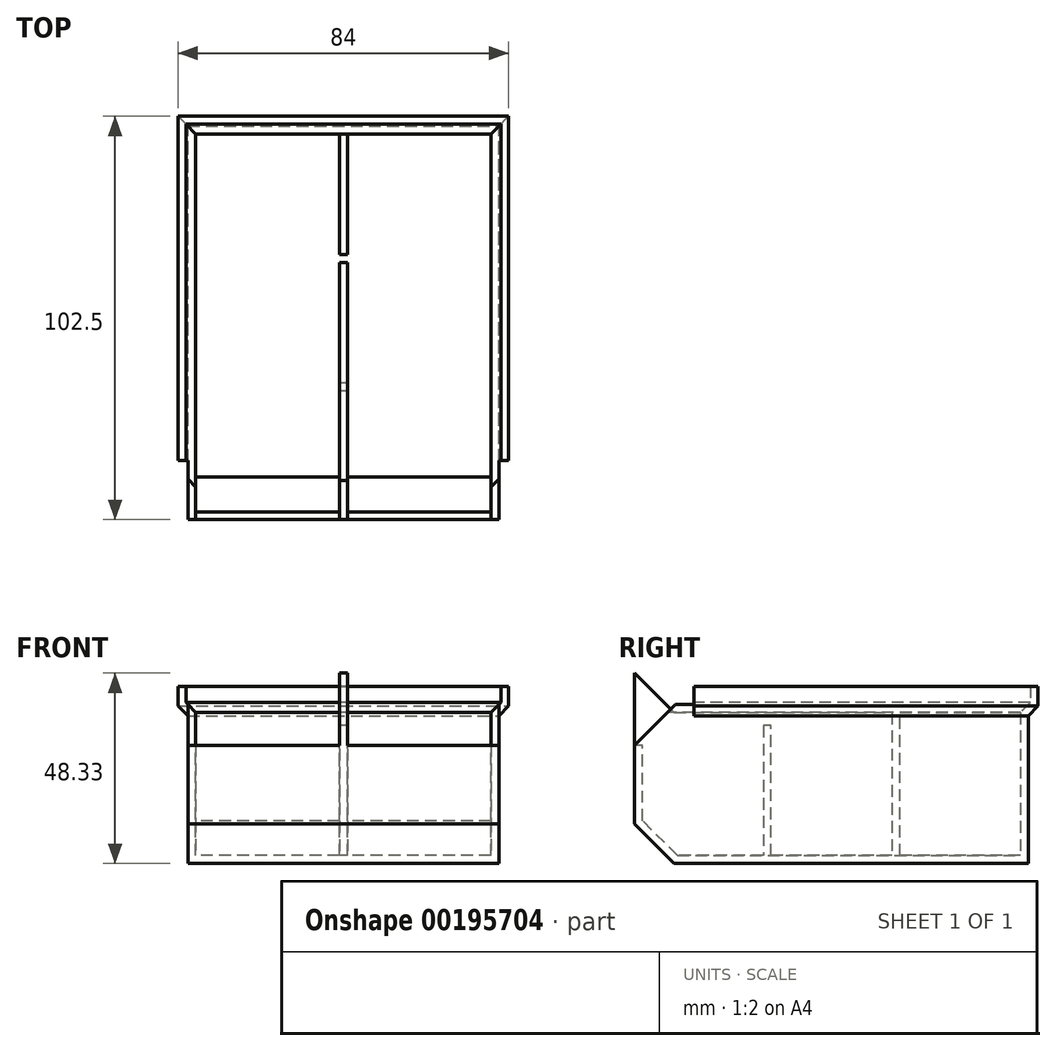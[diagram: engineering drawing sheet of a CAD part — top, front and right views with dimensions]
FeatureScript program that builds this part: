
annotation { "Feature Type Name" : "Feature", "Feature Type Description" : "" }
export const myFeature = defineFeature(function(context is Context, id is Id, definition is map)
    precondition{}
    {
        {
            var Q0;
            Q0=qCreatedBy(makeId("Right.planeOp"),FACE);
            var sketch = newSketch(context, id + "F0", { "sketchPlane" : qUnion([Q0])});
            skLineSegment(sketch, "E0.bottom", {"start": v(0, 0) * mm, "end": v(100, 0) * mm});
            skLineSegment(sketch, "E0.top", {"start": v(0, 45) * mm, "end": v(100, 45) * mm});
            skLineSegment(sketch, "E0.left", {"start": v(0, 0) * mm, "end": v(0, 45) * mm});
            skLineSegment(sketch, "E0.right", {"start": v(100, 0) * mm, "end": v(100, 45) * mm});
            skLineSegment(sketch, "E1", {"start": v(0, 10) * mm, "end": v(10, 0) * mm});
            skLineSegment(sketch, "E2", {"start": v(15, 45) * mm, "end": v(0, 30) * mm});
            skLineSegment(sketch, "E3", {"start": v(100, 45) * mm, "end": v(102.5, 45) * mm});
            skLineSegment(sketch, "E4", {"start": v(102.5, 45) * mm, "end": v(102.5, 40) * mm});
            skLineSegment(sketch, "E5", {"start": v(102.5, 40) * mm, "end": v(100, 37.5) * mm});
            skSolve(sketch);
        }
        {
            var Q0;
            {var subQ4=sQuery(id+"F0.wireOp",EDGE,"E1");Q0=makeQuery(id+"F0.imprint","IMPRINT",FACE,{"disambiguationData":[TD([[makeQuery(id+"F0.imprint","IMPRINT",EDGE,{"derivedFrom":subQ4}),1.0]])]});}
            var Q1;
            {var subQ0=sQuery(id+"F0.wireOp",EDGE,"E3");Q1=makeQuery(id+"F0.imprint","IMPRINT",FACE,{"disambiguationData":[TD([[makeQuery(id+"F0.imprint","IMPRINT",EDGE,{"derivedFrom":subQ0}),-1.0]])]});}
            extrude(context, id + "F1", {"entities" : qUnion([Q0, Q1]), "oppositeDirection" : true, "depth" : 2 * mm});
        }
        {
            var Q0;
            Q0=makeQuery(id+"F1.opExtrude","CAP_FACE",FACE,{"disambiguationData":[OSD([sQuery(id+"F0.wireOp",EDGE,"E0.bottom"),sQuery(id+"F0.wireOp",EDGE,"E0.top"),sQuery(id+"F0.wireOp",EDGE,"E0.left"),sQuery(id+"F0.wireOp",EDGE,"E0.right"),sQuery(id+"F0.wireOp",EDGE,"E1"),sQuery(id+"F0.wireOp",EDGE,"E2"),sQuery(id+"F0.wireOp",EDGE,"E3"),sQuery(id+"F0.wireOp",EDGE,"E4"),sQuery(id+"F0.wireOp",EDGE,"E5")])],"isStart":true});
            var sketch = newSketch(context, id + "F2", { "sketchPlane" : qUnion([Q0])});
            skLineSegment(sketch, "E6", {"start": v(0, 30) * mm, "end": v(2, 30) * mm});
            skLineSegment(sketch, "E7", {"start": v(2, 30) * mm, "end": v(2, 10.83) * mm});
            skLineSegment(sketch, "E8", {"start": v(2, 10.83) * mm, "end": v(10.83, 2) * mm});
            skLineSegment(sketch, "E9", {"start": v(10.83, 2) * mm, "end": v(98, 2) * mm});
            skLineSegment(sketch, "E10", {"start": v(98, 2) * mm, "end": v(98, 38.33) * mm});
            skLineSegment(sketch, "E11", {"start": v(98, 38.33) * mm, "end": v(100.5, 40.83) * mm});
            skPoint(sketch, "E12.0", {"position": v(0, 20) * mm});
            skLineSegment(sketch, "E13.0", {"start": v(0, 10) * mm, "end": v(0, 30) * mm});
            skLineSegment(sketch, "E14.0", {"start": v(0, 10) * mm, "end": v(10, 0) * mm});
            skLineSegment(sketch, "E15.0", {"start": v(10, 0) * mm, "end": v(100, 0) * mm});
            skLineSegment(sketch, "E16.0", {"start": v(100, 0) * mm, "end": v(100, 37.5) * mm});
            skPoint(sketch, "E17.0", {"position": v(101.25, 38.75) * mm});
            skPoint(sketch, "E18.0", {"position": v(102.5, 42.5) * mm});
            skLineSegment(sketch, "E19.0", {"start": v(102.5, 45) * mm, "end": v(102.5, 40) * mm});
            skLineSegment(sketch, "E20.0", {"start": v(102.5, 40) * mm, "end": v(100, 37.5) * mm});
            skLineSegment(sketch, "E21.0", {"start": v(15, 45) * mm, "end": v(102.5, 45) * mm});
            skLineSegment(sketch, "E22", {"start": v(100.5, 40.83) * mm, "end": v(100.5, 45) * mm});
            skLineSegment(sketch, "E23.bottom", {"start": v(32.67, 2) * mm, "end": v(34.67, 2) * mm});
            skLineSegment(sketch, "E23.top", {"start": v(32.67, 35) * mm, "end": v(34.67, 35) * mm});
            skLineSegment(sketch, "E23.left", {"start": v(32.67, 2) * mm, "end": v(32.67, 35) * mm});
            skLineSegment(sketch, "E23.right", {"start": v(34.67, 2) * mm, "end": v(34.67, 35) * mm});
            skLineSegment(sketch, "E24.bottom", {"start": v(65.33, 2) * mm, "end": v(67.33, 2) * mm});
            skLineSegment(sketch, "E24.top", {"start": v(65.33, 40) * mm, "end": v(67.33, 40) * mm});
            skLineSegment(sketch, "E24.left", {"start": v(65.33, 2) * mm, "end": v(65.33, 40) * mm});
            skLineSegment(sketch, "E24.right", {"start": v(67.33, 2) * mm, "end": v(67.33, 40) * mm});
            skSolve(sketch);
        }
        {
            var Q0;
            Q0=makeQuery(id+"F2.imprint","IMPRINT",FACE,{"disambiguationData":[TD([[makeQuery(id+"F2.imprint","IMPRINT",EDGE,{"derivedFrom":sQuery(id+"F2.wireOp",EDGE,"E6")}),-1.0]])]});
            var Q1;
            Q1=makeQuery(id+"F2.imprint","IMPRINT",FACE,{"disambiguationData":[TD([[makeQuery(id+"F2.imprint","IMPRINT",EDGE,{"derivedFrom":sQuery(id+"F2.wireOp",EDGE,"E23.bottom")}),1.0]])]});
            var Q2;
            Q2=makeQuery(id+"F2.imprint","IMPRINT",FACE,{"disambiguationData":[TD([[makeQuery(id+"F2.imprint","IMPRINT",EDGE,{"derivedFrom":sQuery(id+"F2.wireOp",EDGE,"E24.bottom")}),1.0]])]});
            extrude(context, id + "F3", {"entities" : qUnion([Q0, Q1, Q2]), "operationType" : NewBodyOperationType.ADD, "depth" : 75 * mm});
        }
        {
            var Q0;
            Q0=makeQuery(id+"F3.opExtrude","CAP_FACE",FACE,{"disambiguationData":[OSD([sQuery(id+"F2.wireOp",EDGE,"E6"),sQuery(id+"F2.wireOp",EDGE,"E7"),sQuery(id+"F2.wireOp",EDGE,"E8"),sQuery(id+"F2.wireOp",EDGE,"E9"),sQuery(id+"F2.wireOp",EDGE,"E10"),sQuery(id+"F2.wireOp",EDGE,"E11"),sQuery(id+"F2.wireOp",EDGE,"E13.0"),sQuery(id+"F2.wireOp",EDGE,"E14.0"),sQuery(id+"F2.wireOp",EDGE,"E15.0"),sQuery(id+"F2.wireOp",EDGE,"E16.0"),sQuery(id+"F2.wireOp",EDGE,"E19.0"),sQuery(id+"F2.wireOp",EDGE,"E20.0"),sQuery(id+"F2.wireOp",EDGE,"E21.0"),sQuery(id+"F2.wireOp",EDGE,"E22"),sQuery(id+"F2.wireOp",EDGE,"E23.top"),sQuery(id+"F2.wireOp",EDGE,"E23.left"),sQuery(id+"F2.wireOp",EDGE,"E23.right"),sQuery(id+"F2.wireOp",EDGE,"E24.top"),sQuery(id+"F2.wireOp",EDGE,"E24.left"),sQuery(id+"F2.wireOp",EDGE,"E24.right")])],"isStart":false});
            var sketch = newSketch(context, id + "F4", { "sketchPlane" : qUnion([Q0])});
            skLineSegment(sketch, "E25.0", {"start": v(15, 45) * mm, "end": v(0, 30) * mm});
            skLineSegment(sketch, "E26.0", {"start": v(15, 45) * mm, "end": v(100.5, 45) * mm});
            skLineSegment(sketch, "E27.0", {"start": v(100.5, 45) * mm, "end": v(102.5, 45) * mm});
            skLineSegment(sketch, "E28.0", {"start": v(102.5, 45) * mm, "end": v(102.5, 40) * mm});
            skLineSegment(sketch, "E29.0", {"start": v(102.5, 40) * mm, "end": v(100, 37.5) * mm});
            skLineSegment(sketch, "E30.0", {"start": v(100, 0) * mm, "end": v(100, 37.5) * mm});
            skLineSegment(sketch, "E31.0", {"start": v(10, 0) * mm, "end": v(100, 0) * mm});
            skLineSegment(sketch, "E32.0", {"start": v(0, 10) * mm, "end": v(10, 0) * mm});
            skLineSegment(sketch, "E33.0", {"start": v(0, 10) * mm, "end": v(0, 30) * mm});
            skSolve(sketch);
        }
        {
            var Q0;
            Q0 = qSketchRegion(id + "F4", true);
            extrude(context, id + "F5", {"entities" : qUnion([Q0]), "operationType" : NewBodyOperationType.ADD, "depth" : 2 * mm});
        }
        {
            var Q0;
            Q0=makeQuery(id+"F5.boolean.opBoolean","MERGE",FACE,{"derivedFrom":[makeQuery(id+"F3.boolean.opBoolean","MERGE",FACE,{"derivedFrom":[makeQuery(id+"F1.opExtrude","SWEPT_FACE",FACE,{"disambiguationData":[OSD([sQuery(id+"F0.wireOp",EDGE,"E0.top"),sQuery(id+"F0.wireOp",EDGE,"E3")])]}),makeQuery(id+"F3.opExtrude","SWEPT_FACE",FACE,{"disambiguationData":[OSD([sQuery(id+"F2.wireOp",EDGE,"E21.0")])]})]}),makeQuery(id+"F5.opExtrude","SWEPT_FACE",FACE,{"disambiguationData":[OSD([sQuery(id+"F4.wireOp",EDGE,"E26.0"),sQuery(id+"F4.wireOp",EDGE,"E27.0")])]})]});
            var sketch = newSketch(context, id + "F6", { "sketchPlane" : qUnion([Q0])});
            skLineSegment(sketch, "E34.bottom", {"start": v(-2, 102.5) * mm, "end": v(-4.5, 102.5) * mm});
            skLineSegment(sketch, "E34.top", {"start": v(-2, 15) * mm, "end": v(-4.5, 15) * mm});
            skLineSegment(sketch, "E34.left", {"start": v(-2, 102.5) * mm, "end": v(-2, 15) * mm});
            skLineSegment(sketch, "E34.right", {"start": v(-4.5, 102.5) * mm, "end": v(-4.5, 15) * mm});
            skLineSegment(sketch, "E35.bottom", {"start": v(77, 102.5) * mm, "end": v(79.5, 102.5) * mm});
            skLineSegment(sketch, "E35.top", {"start": v(77, 15) * mm, "end": v(79.5, 15) * mm});
            skLineSegment(sketch, "E35.left", {"start": v(77, 102.5) * mm, "end": v(77, 15) * mm});
            skLineSegment(sketch, "E35.right", {"start": v(79.5, 102.5) * mm, "end": v(79.5, 15) * mm});
            skSolve(sketch);
        }
        {
            var Q0;
            Q0 = qSketchRegion(id + "F6", true);
            extrude(context, id + "F7", {"entities" : qUnion([Q0]), "operationType" : NewBodyOperationType.ADD, "oppositeDirection" : true, "depth" : 7.5 * mm});
        }
        {
            var Q0;
            Q0=makeQuery(id+"F7.boolean.opBoolean","MERGE",FACE,{"derivedFrom":[makeQuery(id+"F5.boolean.opBoolean","MERGE",FACE,{"derivedFrom":[makeQuery(id+"F3.boolean.opBoolean","MERGE",FACE,{"derivedFrom":[makeQuery(id+"F1.opExtrude","SWEPT_FACE",FACE,{"disambiguationData":[OSD([sQuery(id+"F0.wireOp",EDGE,"E4")])]}),makeQuery(id+"F3.opExtrude","SWEPT_FACE",FACE,{"disambiguationData":[OSD([sQuery(id+"F2.wireOp",EDGE,"E19.0")])]})]}),makeQuery(id+"F5.opExtrude","SWEPT_FACE",FACE,{"disambiguationData":[OSD([sQuery(id+"F4.wireOp",EDGE,"E28.0")])]})]}),makeQuery(id+"F7.opExtrude","SWEPT_FACE",FACE,{"disambiguationData":[OSD([sQuery(id+"F6.wireOp",EDGE,"E34.bottom")])]}),makeQuery(id+"F7.opExtrude","SWEPT_FACE",FACE,{"disambiguationData":[OSD([sQuery(id+"F6.wireOp",EDGE,"E35.bottom")])]})]});
            var sketch = newSketch(context, id + "F8", { "sketchPlane" : qUnion([Q0])});
            skLineSegment(sketch, "E36", {"start": v(-77, 37.5) * mm, "end": v(-79.5, 40) * mm});
            skLineSegment(sketch, "E37", {"start": v(2, 37.5) * mm, "end": v(4.5, 40) * mm});
            skLineSegment(sketch, "E38.0", {"start": v(-79.5, 37.5) * mm, "end": v(-79.5, 45) * mm});
            skLineSegment(sketch, "E39.0", {"start": v(-77, 37.5) * mm, "end": v(-79.5, 37.5) * mm});
            skLineSegment(sketch, "E40.0", {"start": v(2, 37.5) * mm, "end": v(4.5, 37.5) * mm});
            skLineSegment(sketch, "E41.0", {"start": v(4.5, 37.5) * mm, "end": v(4.5, 45) * mm});
            skSolve(sketch);
        }
        {
            var Q0;
            {var subQ0=sQuery(id+"F8.wireOp",EDGE,"E36");Q0=makeQuery(id+"F8.imprint","IMPRINT",FACE,{"disambiguationData":[TD([[makeQuery(id+"F8.imprint","IMPRINT",EDGE,{"derivedFrom":subQ0}),1.0]])]});}
            var Q1;
            {var subQ0=sQuery(id+"F8.wireOp",EDGE,"E37");Q1=makeQuery(id+"F8.imprint","IMPRINT",FACE,{"disambiguationData":[TD([[makeQuery(id+"F8.imprint","IMPRINT",EDGE,{"derivedFrom":subQ0}),-1.0]])]});}
            extrude(context, id + "F9", {"entities" : qUnion([Q0, Q1]), "operationType" : NewBodyOperationType.REMOVE, "endBound" : BoundingType.THROUGH_ALL, "oppositeDirection" : true, "depth" : 25 * mm});
        }
        {
            var Q0;
            Q0=makeQuery(id+"F7.opExtrude","SWEPT_FACE",FACE,{"disambiguationData":[OSD([sQuery(id+"F6.wireOp",EDGE,"E35.right")])]});
            var sketch = newSketch(context, id + "F10", { "sketchPlane" : qUnion([Q0])});
            skLineSegment(sketch, "E42.0", {"start": v(100, 0) * mm, "end": v(100, 37.5) * mm});
            skLineSegment(sketch, "E43.0", {"start": v(15, 37.5) * mm, "end": v(100, 37.5) * mm});
            skLineSegment(sketch, "E44.0", {"start": v(102.5, 37.5) * mm, "end": v(102.5, 40) * mm});
            skLineSegment(sketch, "E45.0", {"start": v(100, 37.5) * mm, "end": v(102.5, 37.5) * mm});
            skLineSegment(sketch, "E46", {"start": v(102.5, 40) * mm, "end": v(100, 37.5) * mm});
            skSolve(sketch);
        }
        {
            var Q0;
            Q0=makeQuery(id+"F10.imprint","IMPRINT",FACE,{"disambiguationData":[TD([[makeQuery(id+"F10.imprint","IMPRINT",EDGE,{"derivedFrom":sQuery(id+"F10.wireOp",EDGE,"E44.0")}),1.0]])]});
            extrude(context, id + "F11", {"entities" : qUnion([Q0]), "operationType" : NewBodyOperationType.REMOVE, "endBound" : BoundingType.THROUGH_ALL, "oppositeDirection" : true, "depth" : 25 * mm});
        }
        {
            var Q0;
            Q0=makeQuery(id+"F5.boolean.opBoolean","MERGE",FACE,{"derivedFrom":[makeQuery(id+"F3.boolean.opBoolean","MERGE",FACE,{"derivedFrom":[makeQuery(id+"F1.opExtrude","SWEPT_FACE",FACE,{"disambiguationData":[OSD([sQuery(id+"F0.wireOp",EDGE,"E0.left")])]}),makeQuery(id+"F3.opExtrude","SWEPT_FACE",FACE,{"disambiguationData":[OSD([sQuery(id+"F2.wireOp",EDGE,"E13.0")])]})]}),makeQuery(id+"F5.opExtrude","SWEPT_FACE",FACE,{"disambiguationData":[OSD([sQuery(id+"F4.wireOp",EDGE,"E33.0")])]})]});
            var sketch = newSketch(context, id + "F12", { "sketchPlane" : qUnion([Q0])});
            skLineSegment(sketch, "E47.0", {"start": v(-4.5, 40) * mm, "end": v(-4.5, 45) * mm});
            skLineSegment(sketch, "E48.0", {"start": v(-2, 37.5) * mm, "end": v(-4.5, 40) * mm});
            skLineSegment(sketch, "E49.0", {"start": v(75, 45) * mm, "end": v(0, 45) * mm});
            skLineSegment(sketch, "E50.0", {"start": v(-2, 45) * mm, "end": v(0, 45) * mm});
            skLineSegment(sketch, "E51.0", {"start": v(-2, 45) * mm, "end": v(-4.5, 45) * mm});
            skLineSegment(sketch, "E52.0", {"start": v(79.5, 40) * mm, "end": v(77, 37.5) * mm});
            skLineSegment(sketch, "E53.0", {"start": v(79.5, 40) * mm, "end": v(79.5, 45) * mm});
            skLineSegment(sketch, "E54.0", {"start": v(77, 45) * mm, "end": v(79.5, 45) * mm});
            skLineSegment(sketch, "E55.0", {"start": v(77, 45) * mm, "end": v(75, 45) * mm});
            skLineSegment(sketch, "E56", {"start": v(77.5, 45) * mm, "end": v(77.5, 40.83) * mm});
            skLineSegment(sketch, "E57", {"start": v(77.5, 40.83) * mm, "end": v(75.36, 38.68) * mm});
            skLineSegment(sketch, "E58", {"start": v(0, 38.33) * mm, "end": v(-2.5, 40.83) * mm});
            skLineSegment(sketch, "E59", {"start": v(-2.5, 40.83) * mm, "end": v(-2.5, 45) * mm});
            skLineSegment(sketch, "E60.0", {"start": v(75, 38.33) * mm, "end": v(0, 38.33) * mm});
            skPoint(sketch, "E61.0", {"position": v(37.5, 40.83) * mm});
            skLineSegment(sketch, "E62.0", {"start": v(75, 40.83) * mm, "end": v(0, 40.83) * mm});
            skLineSegment(sketch, "E63", {"start": v(75.36, 38.68) * mm, "end": v(75, 38.33) * mm});
            skSolve(sketch);
        }
        {
            var Q0;
            Q0=makeQuery(id+"F12.imprint","IMPRINT",FACE,{"disambiguationData":[TD([[makeQuery(id+"F12.imprint","IMPRINT",EDGE,{"derivedFrom":sQuery(id+"F12.wireOp",EDGE,"E49.0")}),1.0]])]});
            var Q1;
            Q1=makeQuery(id+"F3.opExtrude","SWEPT_FACE",FACE,{"disambiguationData":[OSD([sQuery(id+"F2.wireOp",EDGE,"E10")])]});
            extrude(context, id + "F13", {"entities" : qUnion([Q0]), "operationType" : NewBodyOperationType.REMOVE, "endBound" : BoundingType.UP_TO_SURFACE, "oppositeDirection" : true, "endBoundEntityFace" : qUnion([Q1]), "depth" : 25 * mm});
        }
        {
            var Q0;
            {var subQ1=sQuery(id+"F4.wireOp",EDGE,"E27.0");var subQ2=sQuery(id+"F4.wireOp",EDGE,"E26.0");var subQ3=makeQuery(id+"F5.opExtrude","CAP_FACE",FACE,{"disambiguationData":[OSD([sQuery(id+"F4.wireOp",EDGE,"E25.0"),subQ2,subQ1,sQuery(id+"F4.wireOp",EDGE,"E28.0"),sQuery(id+"F4.wireOp",EDGE,"E29.0"),sQuery(id+"F4.wireOp",EDGE,"E30.0"),sQuery(id+"F4.wireOp",EDGE,"E31.0"),sQuery(id+"F4.wireOp",EDGE,"E32.0"),sQuery(id+"F4.wireOp",EDGE,"E33.0")])],"isStart":true});Q0=makeQuery(id+"F13.boolean.opBoolean","SPLIT",FACE,{"disambiguationData":[TD([makeQuery(id+"F3.opExtrude","SWEPT_FACE",FACE,{"disambiguationData":[OSD([sQuery(id+"F2.wireOp",EDGE,"E21.0")])]})])],"derivedFrom":subQ3});}
            var sketch = newSketch(context, id + "F14", { "sketchPlane" : qUnion([Q0])});
            skPoint(sketch, "E64.0", {"position": v(-99.25, 45) * mm});
            skLineSegment(sketch, "E65.0.0", {"start": v(-98, 38.33) * mm, "end": v(-98, 45) * mm});
            skLineSegment(sketch, "E65.0.1", {"start": v(-98, 45) * mm, "end": v(-100.5, 45) * mm});
            skLineSegment(sketch, "E65.0.2", {"start": v(-100.5, 45) * mm, "end": v(-100.5, 40.83) * mm});
            skLineSegment(sketch, "E65.0.3", {"start": v(-100.5, 40.83) * mm, "end": v(-98, 38.33) * mm});
            skSolve(sketch);
        }
        {
            var Q0;
            Q0=makeQuery(id+"F14.imprint","IMPRINT",FACE,{"disambiguationData":[TD([[makeQuery(id+"F14.imprint","IMPRINT",EDGE,{"derivedFrom":sQuery(id+"F14.wireOp",EDGE,"E65.0.0")}),-1.0]])]});
            var Q1;
            Q1=makeQuery(id+"F13.boolean.opBoolean","COPY",FACE,{"derivedFrom":makeQuery(id+"F13.opExtrude","SWEPT_FACE",FACE,{"disambiguationData":[OSD([sQuery(id+"F12.wireOp",EDGE,"E56")])]})});
            extrude(context, id + "F15", {"entities" : qUnion([Q0]), "operationType" : NewBodyOperationType.REMOVE, "endBound" : BoundingType.UP_TO_SURFACE, "oppositeDirection" : true, "endBoundEntityFace" : qUnion([Q1]), "depth" : 25 * mm});
        }
        {
            var Q0;
            Q0=makeQuery(id+"F15.boolean.opBoolean","COPY",FACE,{"derivedFrom":makeQuery(id+"F15.opExtrude","SWEPT_FACE",FACE,{"disambiguationData":[OSD([sQuery(id+"F14.wireOp",EDGE,"E65.0.0")])]})});
            var sketch = newSketch(context, id + "F16", { "sketchPlane" : qUnion([Q0])});
            skLineSegment(sketch, "E66.0.0", {"start": v(-75, 38.33) * mm, "end": v(-77.5, 40.83) * mm});
            skLineSegment(sketch, "E66.0.1", {"start": v(-77.5, 40.83) * mm, "end": v(-77.5, 38.33) * mm});
            skLineSegment(sketch, "E66.0.2", {"start": v(-77.5, 38.33) * mm, "end": v(-75, 38.33) * mm});
            skSolve(sketch);
        }
        {
            var Q0;
            Q0 = qSketchRegion(id + "F16", true);
            var Q1;
            Q1=makeQuery(id+"F15.boolean.opBoolean","MERGE",FACE,{"derivedFrom":[makeQuery(id+"F3.opExtrude","SWEPT_FACE",FACE,{"disambiguationData":[OSD([sQuery(id+"F2.wireOp",EDGE,"E22")])]}),makeQuery(id+"F15.opExtrude","SWEPT_FACE",FACE,{"disambiguationData":[OSD([sQuery(id+"F14.wireOp",EDGE,"E65.0.2")])]})]});
            extrude(context, id + "F17", {"entities" : qUnion([Q0]), "operationType" : NewBodyOperationType.ADD, "endBound" : BoundingType.UP_TO_SURFACE, "endBoundEntityFace" : qUnion([Q1]), "depth" : 25 * mm});
        }
        {
            var Q0;
            {var subQ1=sQuery(id+"F0.wireOp",EDGE,"E3");var subQ2=sQuery(id+"F0.wireOp",EDGE,"E0.top");var subQ3=makeQuery(id+"F1.opExtrude","CAP_FACE",FACE,{"disambiguationData":[OSD([sQuery(id+"F0.wireOp",EDGE,"E0.bottom"),subQ2,sQuery(id+"F0.wireOp",EDGE,"E0.left"),sQuery(id+"F0.wireOp",EDGE,"E0.right"),sQuery(id+"F0.wireOp",EDGE,"E1"),sQuery(id+"F0.wireOp",EDGE,"E2"),subQ1,sQuery(id+"F0.wireOp",EDGE,"E4"),sQuery(id+"F0.wireOp",EDGE,"E5")])],"isStart":true});Q0=makeQuery(id+"F13.boolean.opBoolean","SPLIT",FACE,{"disambiguationData":[TD([makeQuery(id+"F3.opExtrude","SWEPT_FACE",FACE,{"disambiguationData":[OSD([sQuery(id+"F2.wireOp",EDGE,"E21.0")])]})])],"derivedFrom":subQ3});}
            var sketch = newSketch(context, id + "F18", { "sketchPlane" : qUnion([Q0])});
            skLineSegment(sketch, "E67.0.0", {"start": v(100.5, 45) * mm, "end": v(98, 45) * mm});
            skLineSegment(sketch, "E67.0.1", {"start": v(98, 45) * mm, "end": v(98, 38.33) * mm});
            skLineSegment(sketch, "E67.0.2", {"start": v(98, 38.33) * mm, "end": v(100.5, 40.83) * mm});
            skLineSegment(sketch, "E67.0.3", {"start": v(100.5, 40.83) * mm, "end": v(100.5, 45) * mm});
            skSolve(sketch);
        }
        {
            var Q0;
            Q0=makeQuery(id+"F18.imprint","IMPRINT",FACE,{"disambiguationData":[TD([[makeQuery(id+"F18.imprint","IMPRINT",EDGE,{"derivedFrom":sQuery(id+"F18.wireOp",EDGE,"E67.0.0")}),-1.0]])]});
            var Q1;
            Q1=makeQuery(id+"F13.boolean.opBoolean","COPY",FACE,{"derivedFrom":makeQuery(id+"F13.opExtrude","SWEPT_FACE",FACE,{"disambiguationData":[OSD([sQuery(id+"F12.wireOp",EDGE,"E59")])]})});
            extrude(context, id + "F19", {"entities" : qUnion([Q0]), "operationType" : NewBodyOperationType.REMOVE, "endBound" : BoundingType.UP_TO_SURFACE, "oppositeDirection" : true, "endBoundEntityFace" : qUnion([Q1]), "depth" : 25 * mm});
        }
        {
            var Q0;
            Q0=makeQuery(id+"F19.boolean.opBoolean","COPY",FACE,{"derivedFrom":makeQuery(id+"F19.opExtrude","SWEPT_FACE",FACE,{"disambiguationData":[OSD([sQuery(id+"F18.wireOp",EDGE,"E67.0.1")])]})});
            var sketch = newSketch(context, id + "F20", { "sketchPlane" : qUnion([Q0])});
            skLineSegment(sketch, "E68.0.0", {"start": v(2.5, 40.83) * mm, "end": v(0, 38.33) * mm});
            skLineSegment(sketch, "E68.0.1", {"start": v(0, 38.33) * mm, "end": v(2.5, 38.33) * mm});
            skLineSegment(sketch, "E68.0.2", {"start": v(2.5, 38.33) * mm, "end": v(2.5, 40.83) * mm});
            skSolve(sketch);
        }
        {
            var Q0;
            Q0 = qSketchRegion(id + "F20", true);
            var Q1;
            Q1=makeQuery(id+"F19.boolean.opBoolean","MERGE",FACE,{"derivedFrom":[makeQuery(id+"F15.boolean.opBoolean","MERGE",FACE,{"derivedFrom":[makeQuery(id+"F3.opExtrude","SWEPT_FACE",FACE,{"disambiguationData":[OSD([sQuery(id+"F2.wireOp",EDGE,"E22")])]}),makeQuery(id+"F15.opExtrude","SWEPT_FACE",FACE,{"disambiguationData":[OSD([sQuery(id+"F14.wireOp",EDGE,"E65.0.2")])]})]}),makeQuery(id+"F19.opExtrude","SWEPT_FACE",FACE,{"disambiguationData":[OSD([sQuery(id+"F18.wireOp",EDGE,"E67.0.3")])]})]});
            extrude(context, id + "F21", {"entities" : qUnion([Q0]), "operationType" : NewBodyOperationType.ADD, "endBound" : BoundingType.UP_TO_SURFACE, "endBoundEntityFace" : qUnion([Q1]), "depth" : 25 * mm});
        }
        {
            var Q0;
            {var subQ6=sQuery(id+"F0.wireOp",EDGE,"E0.left");var subQ7=sQuery(id+"F0.wireOp",EDGE,"E2");Q0=makeQuery(id+"F13.boolean.opBoolean","SPLIT",FACE,{"disambiguationData":[TD([makeQuery(id+"F1.opExtrude","SWEPT_FACE",FACE,{"disambiguationData":[OSD([subQ6])]})])],"derivedFrom":makeQuery(id+"F1.opExtrude","CAP_FACE",FACE,{"disambiguationData":[OSD([sQuery(id+"F0.wireOp",EDGE,"E0.bottom"),sQuery(id+"F0.wireOp",EDGE,"E0.top"),subQ6,sQuery(id+"F0.wireOp",EDGE,"E0.right"),sQuery(id+"F0.wireOp",EDGE,"E1"),subQ7,sQuery(id+"F0.wireOp",EDGE,"E3"),sQuery(id+"F0.wireOp",EDGE,"E4"),sQuery(id+"F0.wireOp",EDGE,"E5")])],"isStart":true})});}
            cPlane(context, id + "F22", {"entities" : qUnion([Q0]), "cplaneType" : CPlaneType.OFFSET, "offset" : (75 / 2 - 1) * mm, "width" : 150 * mm, "height" : 150 * mm});
        }
        {
            var Q0;
            Q0=qCreatedBy(id+"F22.planeOp",FACE);
            var sketch = newSketch(context, id + "F23", { "sketchPlane" : qUnion([Q0])});
            skLineSegment(sketch, "E69.0.0", {"start": v(67.33, 38.33) * mm, "end": v(98, 38.33) * mm});
            skLineSegment(sketch, "E69.0.1", {"start": v(98, 38.33) * mm, "end": v(98, 2) * mm});
            skLineSegment(sketch, "E69.0.2", {"start": v(98, 2) * mm, "end": v(67.33, 2) * mm});
            skLineSegment(sketch, "E69.0.3", {"start": v(67.33, 2) * mm, "end": v(67.33, 38.33) * mm});
            skLineSegment(sketch, "E70.0.0", {"start": v(8.33, 38.33) * mm, "end": v(65.33, 38.33) * mm});
            skLineSegment(sketch, "E70.0.1", {"start": v(65.33, 38.33) * mm, "end": v(65.33, 2) * mm});
            skLineSegment(sketch, "E70.0.2", {"start": v(65.33, 2) * mm, "end": v(34.67, 2) * mm});
            skLineSegment(sketch, "E70.0.3", {"start": v(34.67, 2) * mm, "end": v(34.67, 35) * mm});
            skLineSegment(sketch, "E70.0.4", {"start": v(34.67, 35) * mm, "end": v(32.67, 35) * mm});
            skLineSegment(sketch, "E70.0.5", {"start": v(32.67, 35) * mm, "end": v(32.67, 2) * mm});
            skLineSegment(sketch, "E70.0.6", {"start": v(32.67, 2) * mm, "end": v(10.83, 2) * mm});
            skLineSegment(sketch, "E70.0.7", {"start": v(10.83, 2) * mm, "end": v(2, 10.83) * mm});
            skLineSegment(sketch, "E70.0.8", {"start": v(2, 10.83) * mm, "end": v(2, 30) * mm});
            skLineSegment(sketch, "E70.0.9", {"start": v(2, 30) * mm, "end": v(0, 30) * mm});
            skLineSegment(sketch, "E70.0.10", {"start": v(0, 30) * mm, "end": v(8.33, 38.33) * mm});
            skLineSegment(sketch, "E71.0.2", {"start": v(15, 37.5) * mm, "end": v(100, 37.5) * mm});
            skLineSegment(sketch, "E71.0.3", {"start": v(100, 37.5) * mm, "end": v(100, 0) * mm});
            skLineSegment(sketch, "E71.0.4", {"start": v(100, 0) * mm, "end": v(10, 0) * mm});
            skLineSegment(sketch, "E71.0.5", {"start": v(10, 0) * mm, "end": v(0, 10) * mm});
            skLineSegment(sketch, "E71.0.6", {"start": v(0, 10) * mm, "end": v(0, 30) * mm});
            skLineSegment(sketch, "E71.0.7", {"start": v(0, 30) * mm, "end": v(10.33, 40.33) * mm});
            skLineSegment(sketch, "E72", {"start": v(10, 0) * mm, "end": v(10, 40.33) * mm});
            skLineSegment(sketch, "E73", {"start": v(10, 38.33) * mm, "end": v(0, 48.33) * mm});
            skLineSegment(sketch, "E74", {"start": v(0, 48.33) * mm, "end": v(0, 30) * mm});
            skLineSegment(sketch, "E75", {"start": v(2, 30) * mm, "end": v(10, 38.33) * mm});
            skSolve(sketch);
        }
        {
            var Q0;
            {var subQ0=sQuery(id+"F23.wireOp",EDGE,"E69.0.0");Q0=makeQuery(id+"F23.imprint","IMPRINT",FACE,{"disambiguationData":[TD([[makeQuery(id+"F23.imprint","IMPRINT",EDGE,{"derivedFrom":subQ0}),-1.0]])]});}
            var Q1;
            {var subQ0=sQuery(id+"F23.wireOp",EDGE,"E69.0.2");Q1=makeQuery(id+"F23.imprint","IMPRINT",FACE,{"disambiguationData":[TD([[makeQuery(id+"F23.imprint","IMPRINT",EDGE,{"derivedFrom":subQ0}),-1.0]])]});}
            var Q2;
            {var subQ0=sQuery(id+"F23.wireOp",EDGE,"E71.0.2");var subQ1=sQuery(id+"F23.wireOp",EDGE,"E71.0.1");var subQ2=makeQuery(id+"F23.imprint","INTERSECT",VERTEX,{"derivedFrom":[subQ1,subQ0]});Q2=makeQuery(id+"F23.imprint","IMPRINT",FACE,{"disambiguationData":[TD([[makeQuery(id+"F23.imprint","IMPRINT",EDGE,{"disambiguationData":[TD([[subQ2,1.0]])],"derivedFrom":subQ1}),1.0]])]});}
            var Q3;
            {var subQ2=sQuery(id+"F23.wireOp",EDGE,"UUZnglar-myEO-50tu-LRzE-7Zhw624GzhXP");Q3=makeQuery(id+"F23.imprint","IMPRINT",FACE,{"disambiguationData":[TD([[makeQuery(id+"F23.imprint","IMPRINT",EDGE,{"derivedFrom":subQ2}),1.0]])]});}
            var Q4;
            {var subQ0=sQuery(id+"F23.wireOp",EDGE,"E70.0.2");Q4=makeQuery(id+"F23.imprint","IMPRINT",FACE,{"disambiguationData":[TD([[makeQuery(id+"F23.imprint","IMPRINT",EDGE,{"derivedFrom":subQ0}),-1.0]])]});}
            var Q5;
            {var subQ0=sQuery(id+"F23.wireOp",EDGE,"E70.0.8");Q5=makeQuery(id+"F23.imprint","IMPRINT",FACE,{"disambiguationData":[TD([[makeQuery(id+"F23.imprint","IMPRINT",EDGE,{"derivedFrom":subQ0}),-1.0]])]});}
            var Q6;
            {var subQ0=sQuery(id+"F23.wireOp",EDGE,"E70.0.10");Q6=makeQuery(id+"F23.imprint","IMPRINT",FACE,{"disambiguationData":[TD([[makeQuery(id+"F23.imprint","IMPRINT",EDGE,{"derivedFrom":subQ0}),1.0]])]});}
            var Q7;
            Q7=makeQuery(id+"F23.imprint","IMPRINT",FACE,{"disambiguationData":[TD([[makeQuery(id+"F23.imprint","IMPRINT",EDGE,{"derivedFrom":sQuery(id+"F23.wireOp",EDGE,"E70.0.9")}),-1.0]])]});
            var Q8;
            {var subQ1=sQuery(id+"F23.wireOp",EDGE,"E71.0.7");var subQ3=sQuery(id+"F23.wireOp",EDGE,"E73");var subQ4=makeQuery(id+"F23.imprint","INTERSECT",VERTEX,{"derivedFrom":[subQ1,subQ3]});Q8=makeQuery(id+"F23.imprint","IMPRINT",FACE,{"disambiguationData":[TD([[makeQuery(id+"F23.imprint","IMPRINT",EDGE,{"disambiguationData":[TD([[subQ4,1.0]])],"derivedFrom":subQ1}),-1.0]])]});}
            extrude(context, id + "F24", {"entities" : qUnion([Q0, Q1, Q2, Q3, Q4, Q5, Q6, Q7, Q8]), "operationType" : NewBodyOperationType.ADD, "depth" : 2 * mm});
        }
    });
